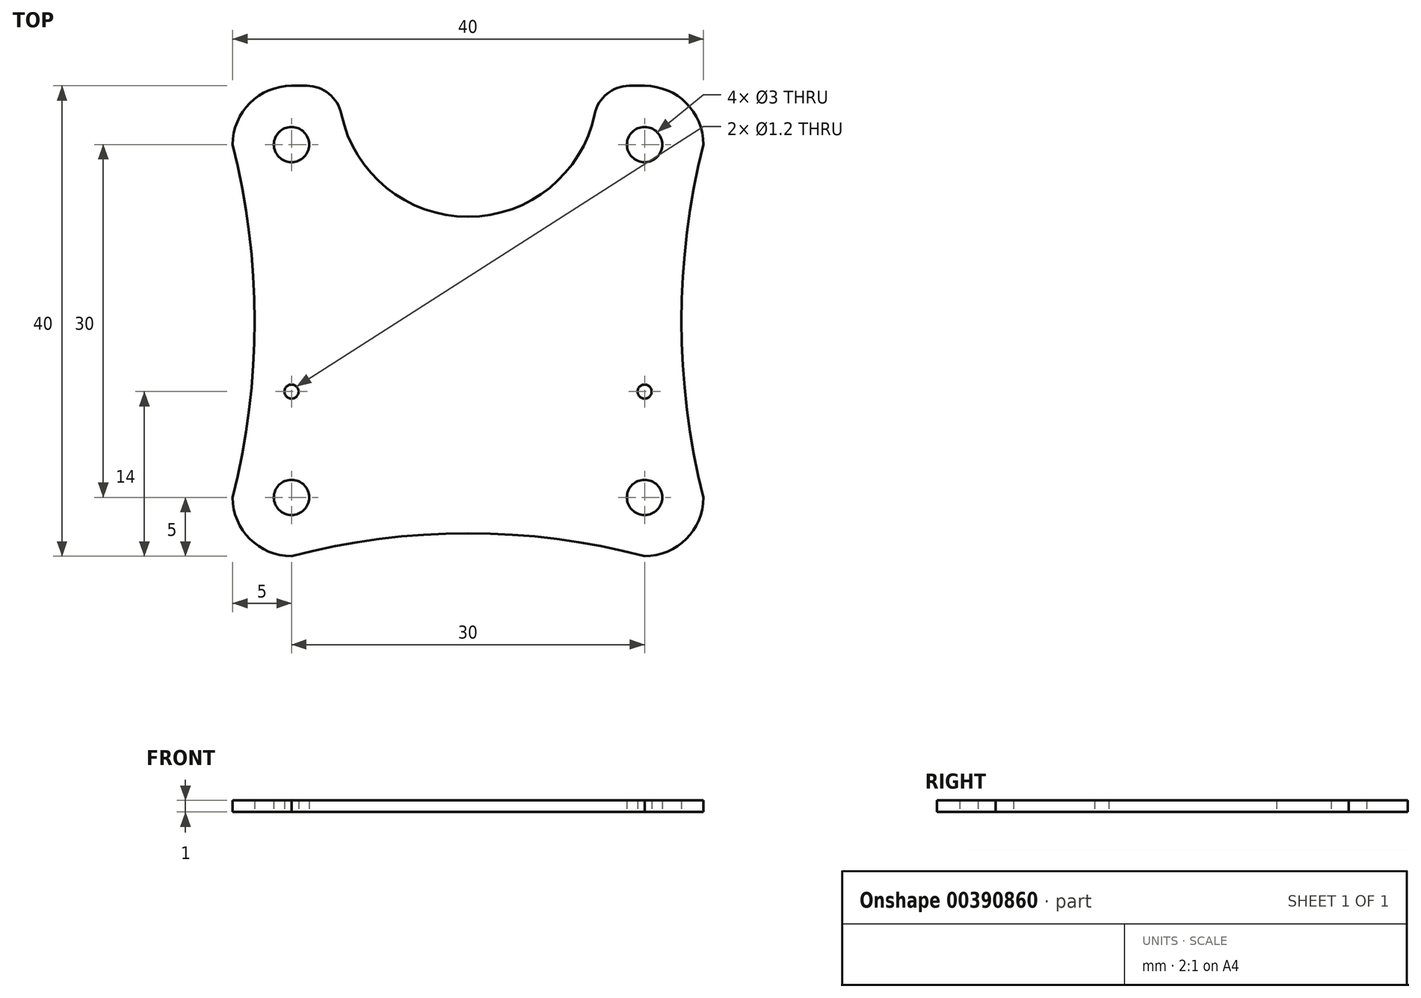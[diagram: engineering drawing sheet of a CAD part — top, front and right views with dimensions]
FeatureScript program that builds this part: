
annotation { "Feature Type Name" : "Feature", "Feature Type Description" : "" }
export const myFeature = defineFeature(function(context is Context, id is Id, definition is map)
    precondition{}
    {
        {
            var Q0;
            Q0=qCreatedBy(makeId("Top.planeOp"),FACE);
            var sketch = newSketch(context, id + "F0", { "sketchPlane" : qUnion([Q0])});
            skPoint(sketch, "E0.middle", {"position": v(0, 0) * mm});
            skCircle(sketch, "E1", {"center": v(-15, 15) * mm, "radius": 1.5 * mm});
            skCircle(sketch, "E2", {"center": v(15, 15) * mm, "radius": 1.5 * mm});
            skCircle(sketch, "E3", {"center": v(15, -15) * mm, "radius": 1.5 * mm});
            skCircle(sketch, "E4", {"center": v(-15, -15) * mm, "radius": 1.5 * mm});
            skLineSegment(sketch, "E5.top", {"start": v(-15, 20) * mm, "end": v(-13.7, 20) * mm});
            skArc(sketch, "E6", {"start": v(-10.77, 17.61) * mm, "mid": v(0, 8.87) * mm, "end": v(10.77, 17.61) * mm});
            skPoint(sketch, "E7.visualSharp", {"position": v(-20, 20) * mm});
            skArc(sketch, "E7.filletArc", {"start": v(-15, 20) * mm, "mid": v(-18.54, 18.54) * mm, "end": v(-20, 15) * mm});
            skLineSegment(sketch, "E8.trimOffspring", {"start": v(13.7, 20) * mm, "end": v(15, 20) * mm});
            skPoint(sketch, "E9.visualSharp", {"position": v(-11, 20) * mm});
            skArc(sketch, "E9.filletArc", {"start": v(-10.77, 17.61) * mm, "mid": v(-11.81, 19.33) * mm, "end": v(-13.7, 20) * mm});
            skPoint(sketch, "E10.visualSharp", {"position": v(11, 20) * mm});
            skArc(sketch, "E10.filletArc", {"start": v(13.7, 20) * mm, "mid": v(11.81, 19.33) * mm, "end": v(10.77, 17.61) * mm});
            skPoint(sketch, "E11.visualSharp", {"position": v(20, 20) * mm});
            skArc(sketch, "E11.filletArc", {"start": v(20, 15) * mm, "mid": v(18.54, 18.54) * mm, "end": v(15, 20) * mm});
            skPoint(sketch, "E12.visualSharp", {"position": v(20, -20) * mm});
            skArc(sketch, "E12.filletArc", {"start": v(15, -20) * mm, "mid": v(18.54, -18.54) * mm, "end": v(20, -15) * mm});
            skPoint(sketch, "E13.visualSharp", {"position": v(-20, -20) * mm});
            skArc(sketch, "E13.filletArc", {"start": v(-20, -15) * mm, "mid": v(-18.54, -18.54) * mm, "end": v(-15, -20) * mm});
            skArc(sketch, "E14", {"start": v(20, 15) * mm, "mid": v(18.14, 0) * mm, "end": v(20, -15) * mm});
            skArc(sketch, "E15.MirrorCS", {"start": v(-20, 15) * mm, "mid": v(-18.14, 0) * mm, "end": v(-20, -15) * mm});
            skArc(sketch, "E16.MirrorCS", {"start": v(-15, -20) * mm, "mid": v(0, -18.05) * mm, "end": v(15, -20) * mm});
            skCircle(sketch, "E17", {"center": v(15, -6) * mm, "radius": 0.6 * mm});
            skCircle(sketch, "E18.MirrorC", {"center": v(-15, -6) * mm, "radius": 0.6 * mm});
            skSolve(sketch);
        }
        {
            var Q0;
            Q0=makeQuery(id+"F0.imprint","IMPRINT",FACE,{"disambiguationData":[TD([[makeQuery(id+"F0.imprint","IMPRINT",EDGE,{"derivedFrom":sQuery(id+"F0.wireOp",EDGE,"E1")}),-1.0]])]});
            extrude(context, id + "F1", {"entities" : qUnion([Q0]), "depth" : 1 * mm, "offsetDistance" : 25 * mm});
        }
    });
